FCSTD DOCUMENT  (FreeCAD 0.20R29410 (Git))
Label: table_530_470
License: All rights reserved
LicenseURL: http://en.wikipedia.org/wiki/All_rights_reserved
objects: Sketcher::SketchObject×1, PartDesign::Body×1
note: 2 computed .brp shape members not serialized (recipe doc carries the construction recipe); baked Part::Feature solids carry a one-line shape summary decoded from their .brp

FEATURE [Sketcher::SketchObject] Sketch
  FullyConstrained = false
  MapMode = 5
  Support = -> [XY_Plane]
  sketch-geometry (5):
    g0: LineSegment StartX=0 StartY=0 StartZ=0 EndX=470 EndY=0 EndZ=0
    g1: LineSegment StartX=470 StartY=0 StartZ=0 EndX=470 EndY=530 EndZ=0
    g2: LineSegment StartX=470 StartY=530 StartZ=0 EndX=0 EndY=530 EndZ=0
    g3: LineSegment StartX=0 StartY=530 StartZ=0 EndX=0 EndY=0 EndZ=0
    g4: Circle CenterX=115 CenterY=467.261 CenterZ=0 NormalX=0 NormalY=0 NormalZ=1 AngleXU=0 Radius=11.4741
  constraints (12):
    c: Coincident(g0,g1)
    c: Coincident(g1,g2)
    c: Coincident(g2,g3)
    c: Coincident(g3,g0)
    c: Horizontal(g0)
    c: Horizontal(g2)
    c: Vertical(g1)
    c: Vertical(g3)
    c: Coincident(g0,g-1)
    c: DistanceY(g1,g1) = 530
    c: DistanceX(g0,g0) = 470
    c: DistanceX(g2,g4) = 115
FEATURE [PartDesign::Body] Body
  Group = -> [Sketch]
  Origin = -> Origin
